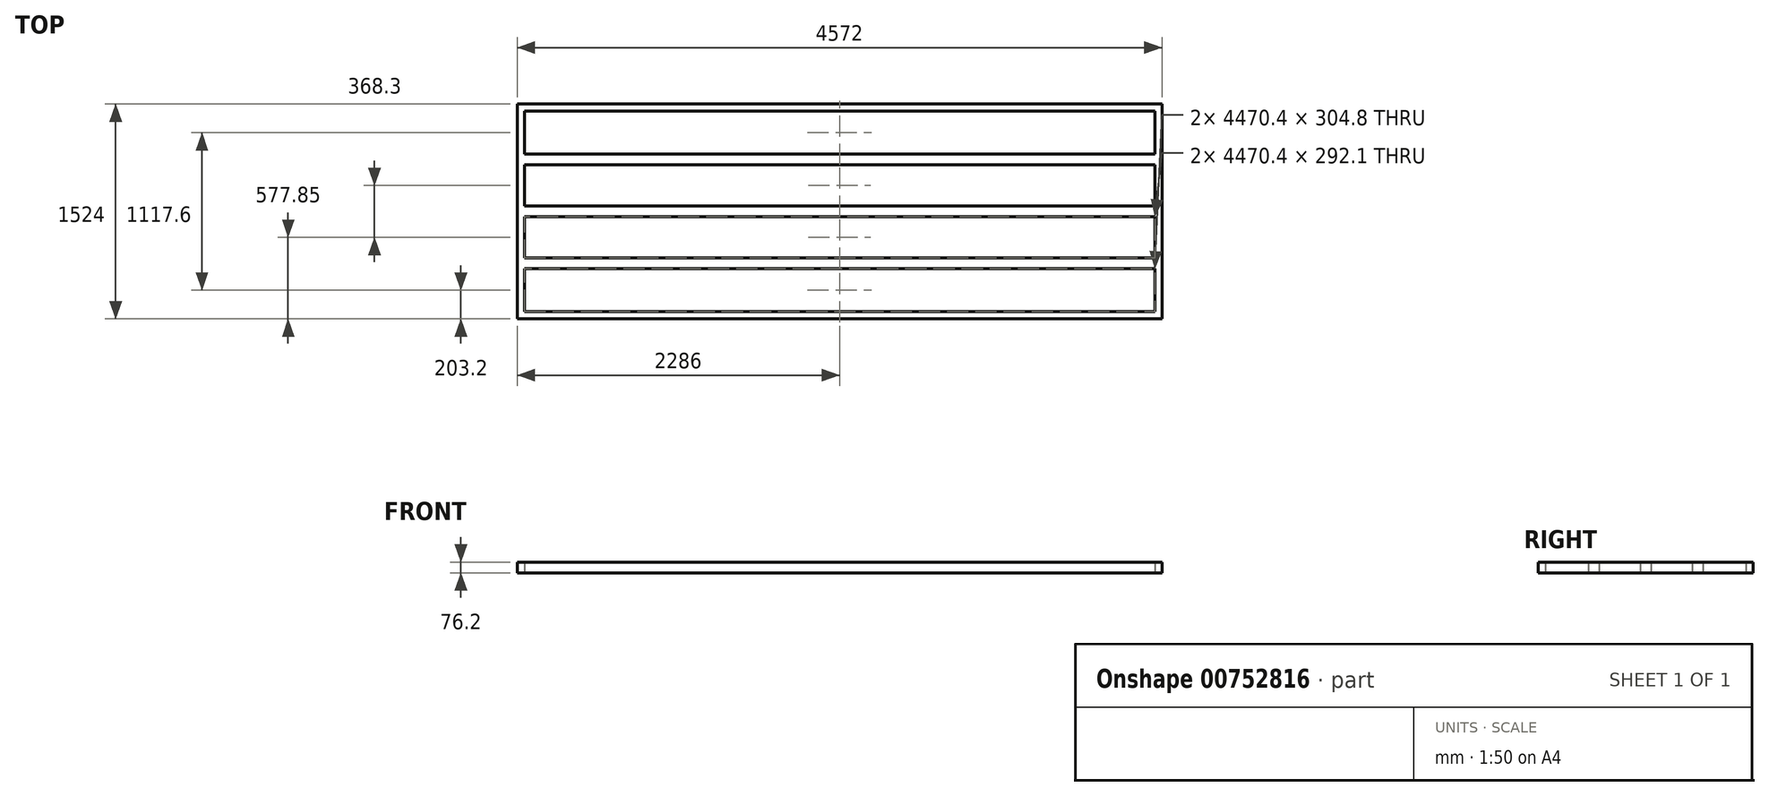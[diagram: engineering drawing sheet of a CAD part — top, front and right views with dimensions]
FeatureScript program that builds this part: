
annotation { "Feature Type Name" : "Feature", "Feature Type Description" : "" }
export const myFeature = defineFeature(function(context is Context, id is Id, definition is map)
    precondition{}
    {
        {
            var Q0;
            Q0=qCreatedBy(makeId("Top.planeOp"),FACE);
            var sketch = newSketch(context, id + "F0", { "sketchPlane" : qUnion([Q0])});
            skLineSegment(sketch, "E0.bottom", {"start": v(-2286, 762) * mm, "end": v(2286, 762) * mm});
            skLineSegment(sketch, "E0.top", {"start": v(-2286, -762) * mm, "end": v(2286, -762) * mm});
            skLineSegment(sketch, "E0.left", {"start": v(-2286, 762) * mm, "end": v(-2286, -762) * mm});
            skLineSegment(sketch, "E0.right", {"start": v(2286, 762) * mm, "end": v(2286, -762) * mm});
            skPoint(sketch, "E0.middle", {"position": v(0, 0) * mm});
            skLineSegment(sketch, "E1.bottom", {"start": v(-2235.2, 711.2) * mm, "end": v(2235.2, 711.2) * mm});
            skLineSegment(sketch, "E1.top", {"start": v(-2235.2, -711.2) * mm, "end": v(2235.2, -711.2) * mm});
            skLineSegment(sketch, "E1.left", {"start": v(-2235.2, 711.2) * mm, "end": v(-2235.2, 406.4) * mm});
            skLineSegment(sketch, "E1.right", {"start": v(2235.2, 711.2) * mm, "end": v(2235.2, 406.4) * mm});
            skLineSegment(sketch, "E2", {"start": v(-2235.2, 406.4) * mm, "end": v(2235.2, 406.4) * mm});
            skLineSegment(sketch, "E3", {"start": v(-2235.2, 330.2) * mm, "end": v(2235.2, 330.2) * mm});
            skLineSegment(sketch, "E4", {"start": v(-2235.2, -38.1) * mm, "end": v(2235.2, -38.1) * mm});
            skLineSegment(sketch, "E5", {"start": v(-2235.2, -330.2) * mm, "end": v(2235.2, -330.2) * mm});
            skLineSegment(sketch, "E6", {"start": v(-2235.2, -406.4) * mm, "end": v(2235.2, -406.4) * mm});
            skLineSegment(sketch, "E7", {"start": v(-2235.2, 38.1) * mm, "end": v(2235.2, 38.1) * mm});
            skLineSegment(sketch, "E8.trimOffspring", {"start": v(-2235.2, 330.2) * mm, "end": v(-2235.2, 38.1) * mm});
            skLineSegment(sketch, "E9.trimOffspring", {"start": v(-2235.2, -38.1) * mm, "end": v(-2235.2, -330.2) * mm});
            skLineSegment(sketch, "E10.trimOffspring", {"start": v(-2235.2, -406.4) * mm, "end": v(-2235.2, -711.2) * mm});
            skLineSegment(sketch, "E11.trimOffspring", {"start": v(2235.2, 330.2) * mm, "end": v(2235.2, 38.1) * mm});
            skLineSegment(sketch, "E12.trimOffspring", {"start": v(2235.2, -38.1) * mm, "end": v(2235.2, -330.2) * mm});
            skLineSegment(sketch, "E13.trimOffspring", {"start": v(2235.2, -406.4) * mm, "end": v(2235.2, -711.2) * mm});
            skSolve(sketch);
        }
        {
            var Q0;
            Q0=makeQuery(id+"F0.imprint","IMPRINT",FACE,{"disambiguationData":[TD([[makeQuery(id+"F0.imprint","IMPRINT",EDGE,{"derivedFrom":sQuery(id+"F0.wireOp",EDGE,"E0.bottom")}),-1.0]])]});
            extrude(context, id + "F1", {"entities" : qUnion([Q0]), "depth" : 76.2 * mm, "offsetDistance" : 25.4 * mm});
        }
    });
